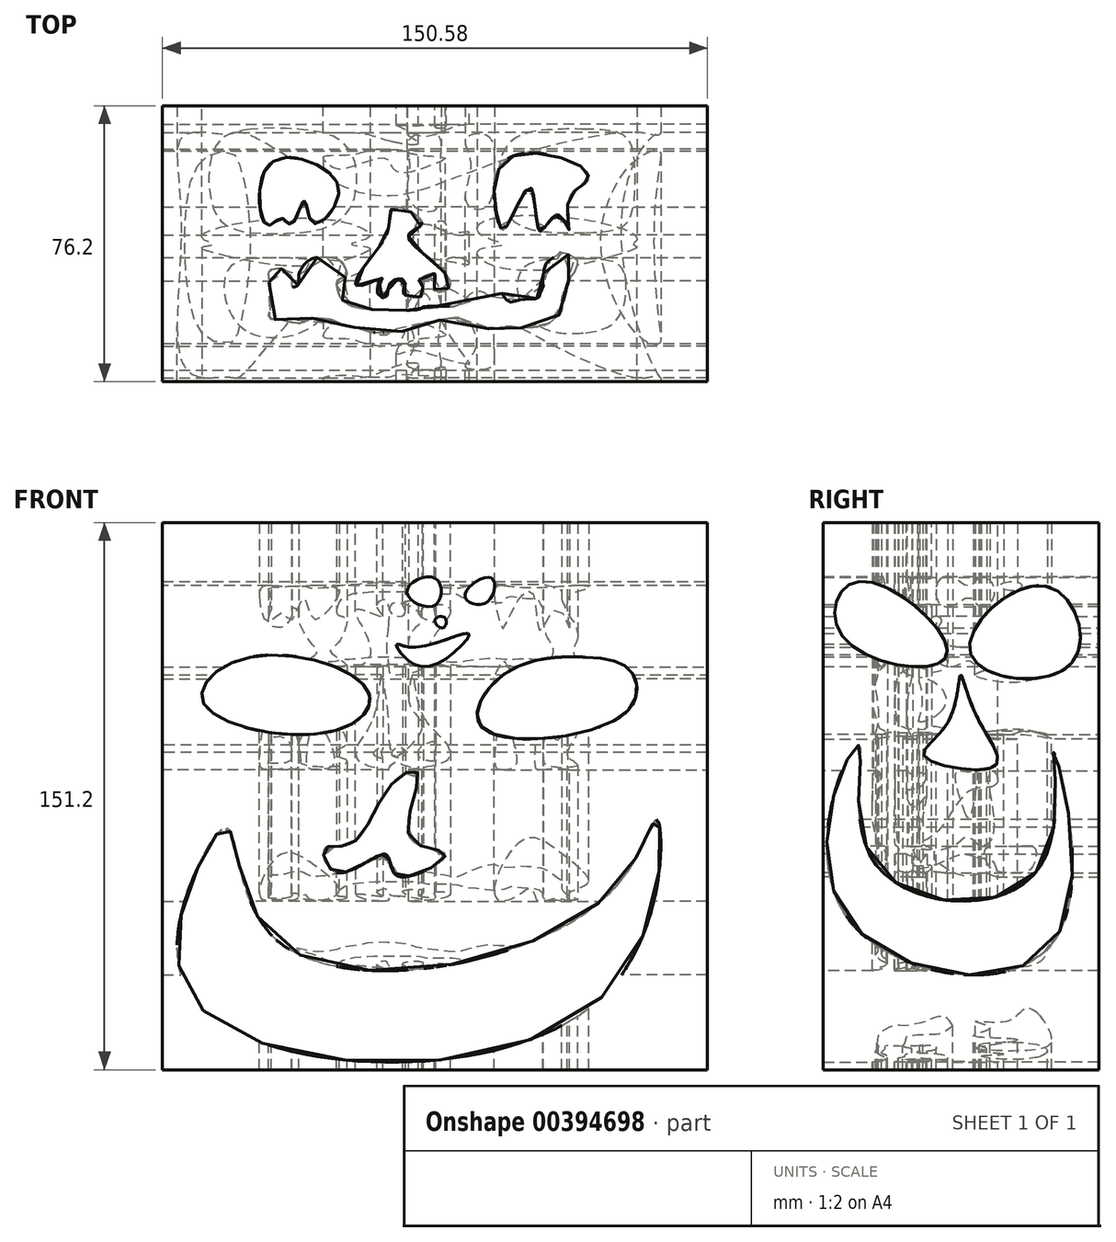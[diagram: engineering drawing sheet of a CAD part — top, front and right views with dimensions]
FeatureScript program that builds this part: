
annotation { "Feature Type Name" : "Feature", "Feature Type Description" : "" }
export const myFeature = defineFeature(function(context is Context, id is Id, definition is map)
    precondition{}
    {
        {
            var Q0;
            Q0=qCreatedBy(makeId("Front.planeOp"),FACE);
            var sketch = newSketch(context, id + "F0", { "sketchPlane" : qUnion([Q0])});
            skLineSegment(sketch, "E0.bottom", {"start": v(-75.29, 75.6) * mm, "end": v(75.29, 75.6) * mm});
            skLineSegment(sketch, "E0.top", {"start": v(-75.29, -75.6) * mm, "end": v(75.29, -75.6) * mm});
            skLineSegment(sketch, "E0.left", {"start": v(-75.29, 75.6) * mm, "end": v(-75.29, -75.6) * mm});
            skLineSegment(sketch, "E0.right", {"start": v(75.29, 75.6) * mm, "end": v(75.29, -75.6) * mm});
            skPoint(sketch, "E0.middle", {"position": v(0, 0) * mm});
            skSolve(sketch);
        }
        {
            var Q0;
            Q0=makeQuery(id+"F0.imprint","IMPRINT",FACE,{"disambiguationData":[TD([[makeQuery(id+"F0.imprint","IMPRINT",EDGE,{"derivedFrom":sQuery(id+"F0.wireOp",EDGE,"E0.bottom")}),-1.0]])]});
            extrude(context, id + "F1", {"entities" : qUnion([Q0]), "depth" : 76.2 * mm});
        }
        {
            var Q0;
            Q0=makeQuery(id+"F1.opExtrude","CAP_FACE",FACE,{"disambiguationData":[OSD([sQuery(id+"F0.wireOp",EDGE,"E0.bottom"),sQuery(id+"F0.wireOp",EDGE,"E0.top"),sQuery(id+"F0.wireOp",EDGE,"E0.left"),sQuery(id+"F0.wireOp",EDGE,"E0.right")])],"isStart":false});
            var sketch = newSketch(context, id + "F2", { "sketchPlane" : qUnion([Q0])});
            skFitSpline(sketch, "E1", {"points": [v(-51.1, 38.43) * mm, v(-64, 25.83) * mm, v(-28.11, 18.04) * mm, v(-18.43, 28.9) * mm, v(-51.1, 38.43) * mm]});
            skFitSpline(sketch, "E2", {"points": [v(41.66, 38.43) * mm, v(19.07, 33.68) * mm, v(13.02, 19.03) * mm, v(52.14, 22.66) * mm, v(54.16, 34.53) * mm, v(41.66, 38.43) * mm]});
            skFitSpline(sketch, "E3", {"points": [v(-11.98, 3.34) * mm, v(-23.27, -13.23) * mm, v(-30.53, -14.52) * mm, v(-26.9, -21.13) * mm, v(-13.6, -16.08) * mm, v(-10.37, -22) * mm, v(2.94, -16.15) * mm, v(-6.74, -11.68) * mm, v(-4.72, 6.24) * mm, v(-11.98, 3.34) * mm]});
            skFitSpline(sketch, "E4", {"points": [v(-65.62, -19.8) * mm, v(-64, -59.27) * mm, v(46.5, -55.2) * mm, v(61.42, -6.52) * mm, v(46.9, -28.06) * mm, v(-43.44, -40.02) * mm, v(-57.15, -8.9) * mm, v(-65.62, -19.8) * mm]});
            skSolve(sketch);
        }
        {
            var Q0;
            Q0 = qSketchRegion(id + "F2", true);
            extrude(context, id + "F3", {"entities" : qUnion([Q0]), "operationType" : NewBodyOperationType.REMOVE, "oppositeDirection" : true, "depth" : 221.74 * mm});
        }
        {
            var Q0;
            Q0=makeQuery(id+"F1.opExtrude","SWEPT_FACE",FACE,{"disambiguationData":[OSD([sQuery(id+"F0.wireOp",EDGE,"E0.right")])]});
            var sketch = newSketch(context, id + "F4", { "sketchPlane" : qUnion([Q0])});
            skFitSpline(sketch, "E5", {"points": [v(-66.16, 59.34) * mm, v(-70.52, 43.8) * mm, v(-42.08, 38.87) * mm, v(-66.16, 59.34) * mm]});
            skFitSpline(sketch, "E6", {"points": [v(-14.59, 58.02) * mm, v(-35.45, 39.44) * mm, v(-7.76, 36.6) * mm, v(-14.59, 58.02) * mm]});
            skFitSpline(sketch, "E7", {"points": [v(-69.57, 10.05) * mm, v(-68.81, -34.5) * mm, v(-12.13, -39.63) * mm, v(-12.5, 12.13) * mm, v(-16.68, -20.1) * mm, v(-61.99, -18.4) * mm, v(-65.97, 13.84) * mm, v(-69.57, 10.05) * mm]});
            skFitSpline(sketch, "E8", {"points": [v(-41.7, 20.48) * mm, v(-48.15, 11) * mm, v(-28.8, 8.34) * mm, v(-33.74, 22) * mm, v(-38.29, 33.56) * mm, v(-41.7, 20.48) * mm]});
            skSolve(sketch);
        }
        {
            var Q0;
            Q0=makeQuery(id+"F4.imprint","IMPRINT",FACE,{"disambiguationData":[TD([[makeQuery(id+"F4.imprint","IMPRINT",EDGE,{"derivedFrom":sQuery(id+"F4.wireOp",EDGE,"E5")}),-1.0]])]});
            var sketch = newSketch(context, id + "F5", { "sketchPlane" : qUnion([Q0])});
            skSolve(sketch);
        }
        {
            var Q0;
            Q0=makeQuery(id+"F4.imprint","IMPRINT",FACE,{"disambiguationData":[TD([[makeQuery(id+"F4.imprint","IMPRINT",EDGE,{"derivedFrom":sQuery(id+"F4.wireOp",EDGE,"E5")}),1.0]])]});
            var Q1;
            Q1=makeQuery(id+"F4.imprint","IMPRINT",FACE,{"disambiguationData":[TD([[makeQuery(id+"F4.imprint","IMPRINT",EDGE,{"derivedFrom":sQuery(id+"F4.wireOp",EDGE,"E6")}),1.0]])]});
            extrude(context, id + "F6", {"entities" : qUnion([Q0, Q1]), "operationType" : NewBodyOperationType.REMOVE, "oppositeDirection" : true, "depth" : 281.7 * mm});
        }
        {
            var Q0;
            Q0 = qSketchRegion(id + "F4", true);
            var Q1;
            Q1=makeQuery(id+"F5.imprint","IMPRINT",FACE,{"disambiguationData":[TD([[makeQuery(id+"F5.imprint","IMPRINT",EDGE,{"derivedFrom":makeQuery(id+"F4.imprint","IMPRINT",EDGE,{"derivedFrom":sQuery(id+"F4.wireOp",EDGE,"E8")})}),1.0]])]});
            extrude(context, id + "F7", {"entities" : qUnion([Q0, Q1]), "operationType" : NewBodyOperationType.REMOVE, "oppositeDirection" : true, "depth" : 283.46 * mm});
        }
        {
            var Q0;
            Q0=makeQuery(id+"F1.opExtrude","SWEPT_FACE",FACE,{"disambiguationData":[OSD([sQuery(id+"F0.wireOp",EDGE,"E0.bottom")])]});
            var sketch = newSketch(context, id + "F8", { "sketchPlane" : qUnion([Q0])});
            skFitSpline(sketch, "E9", {"points": [v(-32.7, -16.3) * mm, v(-46.64, -17.15) * mm, v(-46.36, -33.08) * mm, v(-42.28, -31) * mm, v(-39.72, -32.8) * mm, v(-36.12, -26.25) * mm, v(-33.75, -32.32) * mm, v(-26.64, -25.02) * mm, v(-32.7, -16.3) * mm]});
            skFitSpline(sketch, "E10", {"points": [v(40.2, -16.68) * mm, v(19.05, -15.44) * mm, v(17.92, -33.17) * mm, v(19.34, -33.93) * mm, v(26.35, -22.46) * mm, v(29, -34.6) * mm, v(33.75, -30.14) * mm, v(37.07, -34.21) * mm, v(36.97, -25.87) * mm, v(42.19, -20.66) * mm, v(40.2, -16.68) * mm]});
            skFitSpline(sketch, "E11", {"points": [v(-12.9, -33.83) * mm, v(-17.35, -41.42) * mm, v(-21.61, -49.76) * mm, v(-14.4, -47.58) * mm, v(-16.02, -51) * mm, v(-13.65, -53.17) * mm, v(-12.42, -49.1) * mm, v(-8.91, -47.86) * mm, v(-8.25, -49.57) * mm, v(-8.82, -51.85) * mm, v(-4.36, -52.89) * mm, v(-3.22, -51.75) * mm, v(-3.89, -49.2) * mm, v(-4.55, -48.34) * mm, v(0, -46.35) * mm, v(0, -50.9) * mm, v(3.98, -50.14) * mm, v(0, -43.5) * mm, v(-7.2, -35.54) * mm, v(-3.6, -32.32) * mm, v(-11.38, -28.05) * mm, v(-12.9, -33.83) * mm]});
            skFitSpline(sketch, "E12", {"points": [v(-45.88, -48.72) * mm, v(-45.31, -54.12) * mm, v(-45.88, -58.67) * mm, v(-42.66, -59.15) * mm, v(-37.54, -60.1) * mm, v(-35.27, -59.15) * mm, v(-34.13, -58.67) * mm, v(-27.59, -59.43) * mm, v(-26.16, -60.47) * mm, v(-21.05, -61.52) * mm, v(-17.63, -62.56) * mm, v(-9.86, -62.37) * mm, v(-7.96, -62.18) * mm, v(-5.12, -60.57) * mm, v(-1.7, -59.8) * mm, v(6.45, -58.48) * mm, v(7.68, -59.15) * mm, v(15.45, -61.7) * mm, v(18.01, -61.23) * mm, v(21.42, -61.04) * mm, v(22.28, -61.23) * mm, v(26.16, -61.23) * mm, v(31, -60.38) * mm, v(33.65, -58.3) * mm, v(34.89, -57.06) * mm, v(34.98, -53.65) * mm, v(35.36, -52.04) * mm, v(37.35, -47.4) * mm, v(38.4, -46.16) * mm, v(39.34, -43.88) * mm, v(39.25, -42.65) * mm, v(34.7, -40.38) * mm, v(34.03, -41.04) * mm, v(31, -43.22) * mm, v(29.96, -46.73) * mm, v(29.77, -48.62) * mm, v(29.86, -49.86) * mm, v(28.91, -52.22) * mm, v(28.53, -53.08) * mm, v(23.42, -53.65) * mm, v(20.38, -54.12) * mm, v(18.68, -51.94) * mm, v(18.49, -51.75) * mm, v(10.62, -53.46) * mm, v(9.57, -53.65) * mm, v(7.58, -53.93) * mm, v(6.26, -55.16) * mm, v(4.83, -55.45) * mm, v(2.28, -55.35) * mm, v(0.95, -55.35) * mm, v(-1.14, -55.35) * mm, v(-1.8, -55.35) * mm, v(-3.5, -55.73) * mm, v(-4.27, -56.2) * mm, v(-9.1, -56.5) * mm, v(-9.2, -56.5) * mm, v(-13.56, -56.4) * mm, v(-14.12, -56.4) * mm, v(-17.44, -56.3) * mm, v(-20.95, -55.83) * mm, v(-22.56, -55.54) * mm, v(-24.36, -54.6) * mm, v(-25.97, -53.27) * mm, v(-26.64, -51.75) * mm, v(-26.83, -51.09) * mm, v(-26.92, -48.24) * mm, v(-24.55, -47.1) * mm, v(-25.7, -43.22) * mm, v(-28.82, -41.9) * mm, v(-34.41, -42.46) * mm, v(-37.35, -45.87) * mm, v(-37.64, -47.67) * mm, v(-37.82, -49.48) * mm, v(-39.44, -50.04) * mm, v(-39.53, -48.05) * mm, v(-41.05, -45.68) * mm, v(-42.37, -45.02) * mm, v(-43.99, -45.02) * mm, v(-45.98, -46.06) * mm, v(-45.31, -49.57) * mm, v(-45.88, -48.72) * mm]});
            skSolve(sketch);
        }
        {
            var Q0;
            Q0 = qSketchRegion(id + "F8", true);
            extrude(context, id + "F9", {"entities" : qUnion([Q0]), "operationType" : NewBodyOperationType.REMOVE, "oppositeDirection" : true, "depth" : 257.3 * mm});
        }
        {
            var Q0;
            Q0=makeQuery(id+"F1.opExtrude","CAP_FACE",FACE,{"disambiguationData":[OSD([sQuery(id+"F0.wireOp",EDGE,"E0.bottom"),sQuery(id+"F0.wireOp",EDGE,"E0.top"),sQuery(id+"F0.wireOp",EDGE,"E0.left"),sQuery(id+"F0.wireOp",EDGE,"E0.right")])],"isStart":false});
            var sketch = newSketch(context, id + "F10", { "sketchPlane" : qUnion([Q0])});
            skFitSpline(sketch, "E13", {"points": [v(0, 60.3) * mm, v(-7.76, 56.49) * mm, v(0, 52.83) * mm, v(0, 60.3) * mm]});
            skFitSpline(sketch, "E14", {"points": [v(15.58, 60.3) * mm, v(8.29, 55.57) * mm, v(14.12, 53.47) * mm, v(15.58, 60.3) * mm]});
            skFitSpline(sketch, "E15", {"points": [v(-10.68, 41.93) * mm, v(-6.3, 36.78) * mm, v(3.03, 38.01) * mm, v(9.45, 44.83) * mm, v(3.03, 43.26) * mm, v(-7.76, 41.32) * mm, v(-10.68, 41.93) * mm]});
            skFitSpline(sketch, "E16", {"points": [v(0, 48.76) * mm, v(2.16, 46.51) * mm, v(2.74, 49.3) * mm, v(0, 48.76) * mm]});
            skSolve(sketch);
        }
        {
            var Q0;
            Q0 = qSketchRegion(id + "F10", true);
            extrude(context, id + "F11", {"entities" : qUnion([Q0]), "operationType" : NewBodyOperationType.REMOVE, "oppositeDirection" : true, "depth" : 184.66 * mm});
        }
    });
